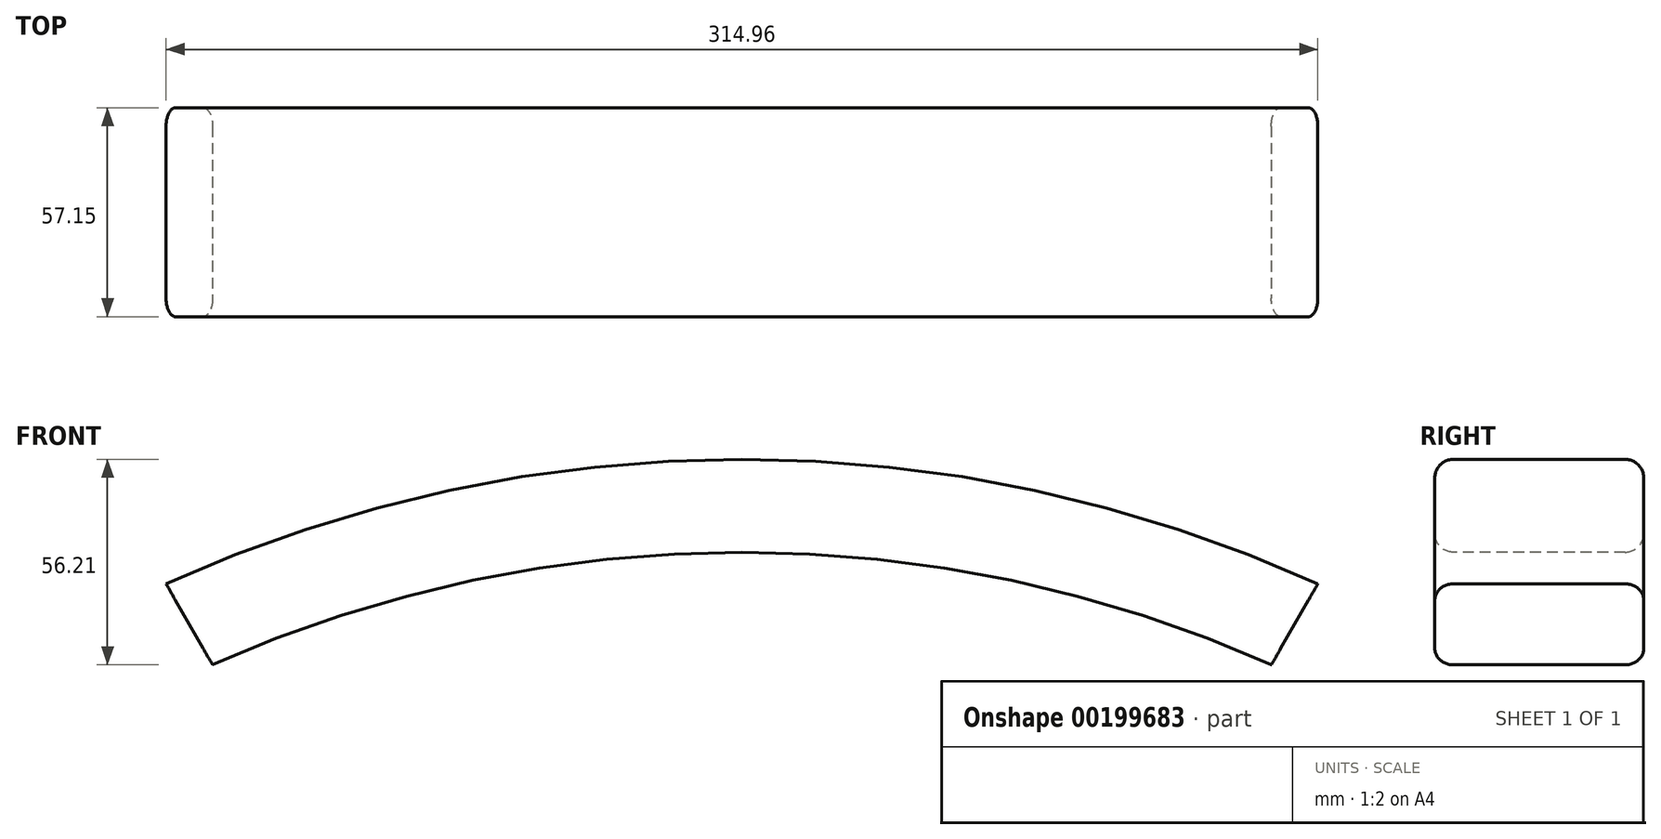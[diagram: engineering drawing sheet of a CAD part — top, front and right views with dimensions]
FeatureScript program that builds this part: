
annotation { "Feature Type Name" : "Feature", "Feature Type Description" : "" }
export const myFeature = defineFeature(function(context is Context, id is Id, definition is map)
    precondition{}
    {
        {
            var Q0;
            Q0=qCreatedBy(makeId("Front.planeOp"),FACE);
            var sketch = newSketch(context, id + "F0", { "sketchPlane" : qUnion([Q0])});
            skArc(sketch, "E0", {"start": v(157.48, 346.93) * mm, "mid": v(0, 381) * mm, "end": v(-157.48, 346.93) * mm});
            skArc(sketch, "E1.0", {"start": v(144.78, 324.8) * mm, "mid": v(0, 355.6) * mm, "end": v(-144.78, 324.8) * mm});
            skLineSegment(sketch, "E2", {"start": v(0, 381) * mm, "end": v(0, -381) * mm, "construction": true});
            skPoint(sketch, "E3", {"position": v(-157.48, 346.93) * mm});
            skPoint(sketch, "E4", {"position": v(157.48, 346.93) * mm});
            skLineSegment(sketch, "E5", {"start": v(-157.48, 346.93) * mm, "end": v(-144.78, 324.8) * mm});
            skLineSegment(sketch, "E6", {"start": v(157.48, 346.93) * mm, "end": v(144.78, 324.8) * mm});
            skSolve(sketch);
        }
        {
            var Q0;
            Q0=makeQuery(id+"F0.imprint","IMPRINT",FACE,{"disambiguationData":[TD([[makeQuery(id+"F0.imprint","IMPRINT",EDGE,{"derivedFrom":sQuery(id+"F0.wireOp",EDGE,"E0")}),1.0]])]});
            extrude(context, id + "F1", {"entities" : qUnion([Q0]), "oppositeDirection" : true, "depth" : 57.15 * mm});
        }
        {
            var Q0;
            Q0=makeQuery(id+"F1.opExtrude","CAP_EDGE",EDGE,{"disambiguationData":[OSD([sQuery(id+"F0.wireOp",EDGE,"E1.0")])],"isStart":true});
            var Q1;
            Q1=makeQuery(id+"F1.opExtrude","CAP_EDGE",EDGE,{"disambiguationData":[OSD([sQuery(id+"F0.wireOp",EDGE,"E0")])],"isStart":true});
            var Q2;
            Q2=makeQuery(id+"F1.opExtrude","CAP_EDGE",EDGE,{"disambiguationData":[OSD([sQuery(id+"F0.wireOp",EDGE,"E0")])],"isStart":false});
            var Q3;
            Q3=makeQuery(id+"F1.opExtrude","CAP_EDGE",EDGE,{"disambiguationData":[OSD([sQuery(id+"F0.wireOp",EDGE,"E1.0")])],"isStart":false});
            fillet(context, id + "F2", {"entities" : qUnion([Q0, Q1, Q2, Q3]), "radius" : 5.08 * mm, "tangentPropagation" : true, "allowEdgeOverflow" : false});
        }
    });
